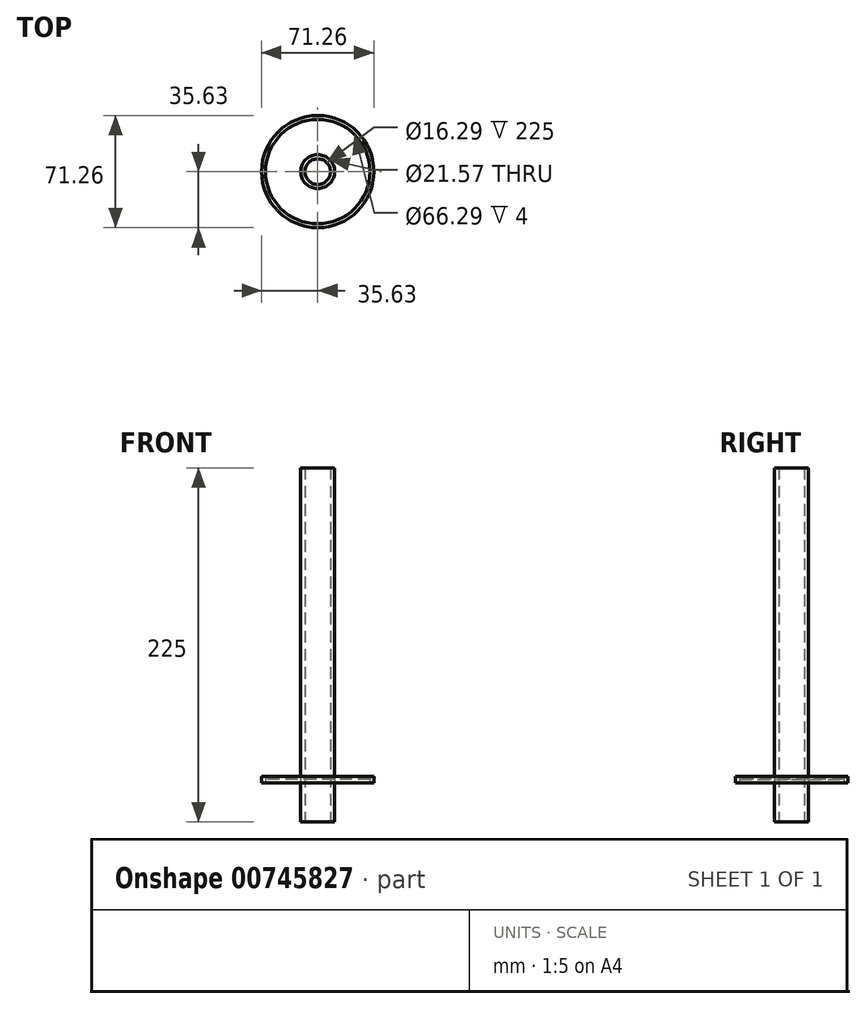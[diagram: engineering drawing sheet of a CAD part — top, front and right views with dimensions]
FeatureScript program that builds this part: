
annotation { "Feature Type Name" : "Feature", "Feature Type Description" : "" }
export const myFeature = defineFeature(function(context is Context, id is Id, definition is map)
    precondition{}
    {
        {
            var Q0;
            Q0=qCreatedBy(makeId("Top.planeOp"),FACE);
            var sketch = newSketch(context, id + "F0", { "sketchPlane" : qUnion([Q0])});
            skCircle(sketch, "E0", {"center": v(0, 0) * mm, "radius": 35.63 * mm});
            skCircle(sketch, "E1", {"center": v(0, 0) * mm, "radius": 10.79 * mm});
            skCircle(sketch, "E2", {"center": v(0, 0) * mm, "radius": 8.14 * mm});
            skCircle(sketch, "E3", {"center": v(0, 0) * mm, "radius": 33.15 * mm});
            skSolve(sketch);
        }
        {
            var Q0;
            Q0=makeQuery(id+"F0.imprint","IMPRINT",FACE,{"disambiguationData":[TD([[makeQuery(id+"F0.imprint","IMPRINT",EDGE,{"derivedFrom":sQuery(id+"F0.wireOp",EDGE,"E0")}),1.0]])]});
            extrude(context, id + "F1", {"entities" : qUnion([Q0]), "depth" : 4 * mm, "offsetDistance" : 25.4 * mm});
        }
        {
            var Q0;
            Q0=makeQuery(id+"F0.imprint","IMPRINT",FACE,{"disambiguationData":[TD([[makeQuery(id+"F0.imprint","IMPRINT",EDGE,{"derivedFrom":sQuery(id+"F0.wireOp",EDGE,"E1")}),1.0]])]});
            extrude(context, id + "F2", {"entities" : qUnion([Q0]), "operationType" : NewBodyOperationType.ADD, "depth" : 200 * mm, "offsetDistance" : 25 * mm, "hasSecondDirection" : true, "secondDirectionOppositeDirection" : true, "secondDirectionDepth" : 25 * mm});
        }
        {
            var Q0;
            Q0=makeQuery(id+"F0.imprint","IMPRINT",FACE,{"disambiguationData":[TD([[makeQuery(id+"F0.imprint","IMPRINT",EDGE,{"derivedFrom":sQuery(id+"F0.wireOp",EDGE,"E1")}),-1.0]])]});
            extrude(context, id + "F3", {"entities" : qUnion([Q0]), "depth" : 2 * mm, "offsetDistance" : 25 * mm});
        }
    });
